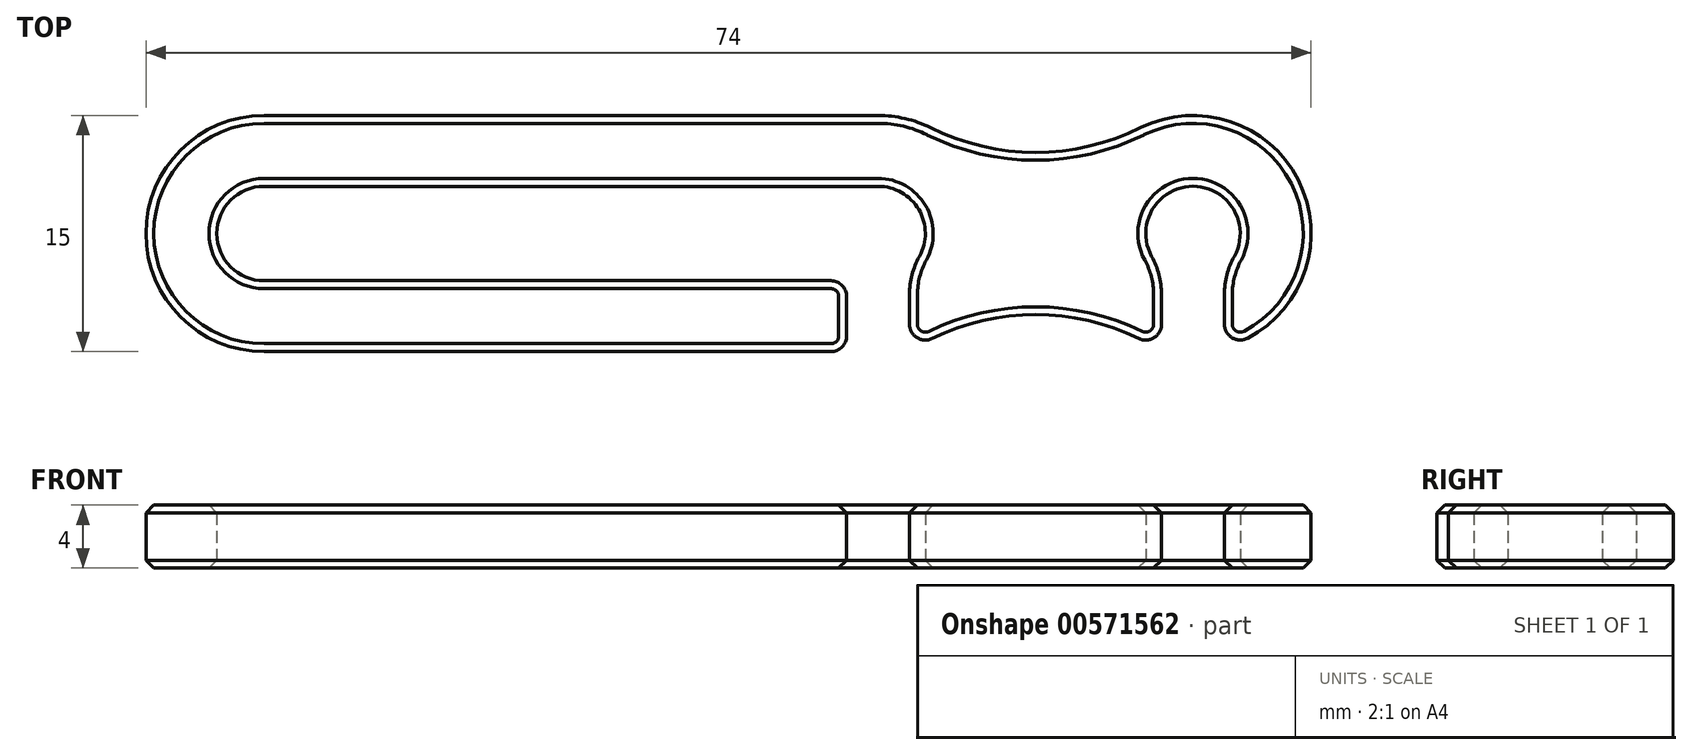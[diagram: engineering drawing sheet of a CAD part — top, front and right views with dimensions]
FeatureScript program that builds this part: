
annotation { "Feature Type Name" : "Feature", "Feature Type Description" : "" }
export const myFeature = defineFeature(function(context is Context, id is Id, definition is map)
    precondition{}
    {
        {
            var Q0;
            Q0=qCreatedBy(makeId("Top.planeOp"),FACE);
            var sketch = newSketch(context, id + "F0", { "sketchPlane" : qUnion([Q0])});
            skArc(sketch, "E0", {"start": v(2, -2.24) * mm, "mid": v(2.8, 1.07) * mm, "end": v(0, 3) * mm});
            skArc(sketch, "E1", {"start": v(-39, 3) * mm, "mid": v(-42, 0) * mm, "end": v(-39, -3) * mm});
            skArc(sketch, "E2", {"start": v(22, -2.24) * mm, "mid": v(20, 3) * mm, "end": v(18, -2.24) * mm});
            skLineSegment(sketch, "E3", {"start": v(23, 6.87) * mm, "end": v(23, -6.87) * mm, "construction": true});
            skLineSegment(sketch, "E4", {"start": v(-42, 6.87) * mm, "end": v(-42, -6.87) * mm, "construction": true});
            skLineSegment(sketch, "E5", {"start": v(-3, 7.5) * mm, "end": v(-3, -7.5) * mm, "construction": true});
            skLineSegment(sketch, "E6", {"start": v(0, 0) * mm, "end": v(-39, 0) * mm, "construction": true});
            skLineSegment(sketch, "E7", {"start": v(0, 0) * mm, "end": v(20, 0) * mm, "construction": true});
            skArc(sketch, "E8", {"start": v(3.33, 6.72) * mm, "mid": v(1.71, 7.3) * mm, "end": v(0, 7.5) * mm, "construction": true});
            skArc(sketch, "E9", {"start": v(16.67, -6.72) * mm, "mid": v(17.32, -7) * mm, "end": v(18, -7.23) * mm, "construction": true});
            skArc(sketch, "E10", {"start": v(-39, 7.5) * mm, "mid": v(-46.5, 0) * mm, "end": v(-39, -7.5) * mm, "construction": true});
            skArc(sketch, "E11", {"start": v(3.33, 6.72) * mm, "mid": v(10, 5.16) * mm, "end": v(16.67, 6.72) * mm, "construction": true});
            skArc(sketch, "E12", {"start": v(16.67, -6.72) * mm, "mid": v(10, -5.16) * mm, "end": v(3.33, -6.72) * mm, "construction": true});
            skLineSegment(sketch, "E13", {"start": v(-39, 7.5) * mm, "end": v(0, 7.5) * mm, "construction": true});
            skLineSegment(sketch, "E14", {"start": v(0, -7.5) * mm, "end": v(-39, -7.5) * mm, "construction": true});
            skArc(sketch, "E15.trimOffspring", {"start": v(0, -7.5) * mm, "mid": v(1.71, -7.3) * mm, "end": v(3.33, -6.72) * mm, "construction": true});
            skLineSegment(sketch, "E16", {"start": v(2, -2.24) * mm, "end": v(2, -7.23) * mm});
            skLineSegment(sketch, "E17", {"start": v(-2, -3) * mm, "end": v(-2, -7.5) * mm});
            skLineSegment(sketch, "E18", {"start": v(0, 0) * mm, "end": v(0, -7.5) * mm, "construction": true});
            skLineSegment(sketch, "E19", {"start": v(-2, -3) * mm, "end": v(-39, -3) * mm});
            skLineSegment(sketch, "E20", {"start": v(-39, 3) * mm, "end": v(0, 3) * mm});
            skPoint(sketch, "E21.orphan", {"position": v(0, -3) * mm});
            skPoint(sketch, "E22.orphan", {"position": v(-2, -2.24) * mm});
            skLineSegment(sketch, "E23", {"start": v(-2, -7.5) * mm, "end": v(-39, -7.5) * mm});
            skLineSegment(sketch, "E24", {"start": v(-39, 7.5) * mm, "end": v(0, 7.5) * mm});
            skArc(sketch, "E25", {"start": v(3.33, 6.72) * mm, "mid": v(1.71, 7.3) * mm, "end": v(0, 7.5) * mm});
            skArc(sketch, "E26", {"start": v(3.33, 6.72) * mm, "mid": v(10, 5.16) * mm, "end": v(16.67, 6.72) * mm});
            skArc(sketch, "E27", {"start": v(16.67, -6.72) * mm, "mid": v(17.32, -7) * mm, "end": v(18, -7.23) * mm});
            skArc(sketch, "E28", {"start": v(16.67, -6.72) * mm, "mid": v(10, -5.16) * mm, "end": v(3.33, -6.72) * mm});
            skArc(sketch, "E29", {"start": v(2, -7.23) * mm, "mid": v(2.68, -7) * mm, "end": v(3.33, -6.72) * mm});
            skArc(sketch, "E30", {"start": v(-39, 7.5) * mm, "mid": v(-46.5, 0) * mm, "end": v(-39, -7.5) * mm});
            skLineSegment(sketch, "E31", {"start": v(20, 0) * mm, "end": v(20, -7.5) * mm, "construction": true});
            skLineSegment(sketch, "E32", {"start": v(18, -2.24) * mm, "end": v(18, -7.23) * mm});
            skLineSegment(sketch, "E33", {"start": v(22, -2.24) * mm, "end": v(22, -7.23) * mm});
            skArc(sketch, "E34.trimOffspring", {"start": v(22, -7.23) * mm, "mid": v(27, 2.68) * mm, "end": v(16.67, 6.72) * mm, "construction": true});
            skArc(sketch, "E35.trimOffspring", {"start": v(22, -7.23) * mm, "mid": v(27, 2.68) * mm, "end": v(16.67, 6.72) * mm});
            skLineSegment(sketch, "E36", {"start": v(27.5, 11.34) * mm, "end": v(27.5, -10.06) * mm, "construction": true});
            skLineSegment(sketch, "E37", {"start": v(-46.5, 12.68) * mm, "end": v(-46.5, -19.11) * mm, "construction": true});
            skSolve(sketch);
        }
        {
            var Q0;
            Q0=makeQuery(id+"F0.imprint","IMPRINT",FACE,{"disambiguationData":[TD([[makeQuery(id+"F0.imprint","IMPRINT",EDGE,{"derivedFrom":sQuery(id+"F0.wireOp",EDGE,"E0")}),-1.0]])]});
            extrude(context, id + "F1", {"entities" : qUnion([Q0]), "depth" : 4 * mm, "offsetDistance" : 25 * mm});
        }
        {
            var Q0;
            Q0=makeQuery(id+"F1.opExtrude","SWEPT_EDGE",EDGE,{"disambiguationData":[OSD([sQuery(id+"F0.wireOp",EDGE,"E0"),sQuery(id+"F0.wireOp",EDGE,"E16")])]});
            var Q1;
            Q1=makeQuery(id+"F1.opExtrude","SWEPT_EDGE",EDGE,{"disambiguationData":[OSD([sQuery(id+"F0.wireOp",EDGE,"E2"),sQuery(id+"F0.wireOp",EDGE,"E32")])]});
            var Q2;
            Q2=makeQuery(id+"F1.opExtrude","SWEPT_EDGE",EDGE,{"disambiguationData":[OSD([sQuery(id+"F0.wireOp",EDGE,"E2"),sQuery(id+"F0.wireOp",EDGE,"E33")])]});
            fillet(context, id + "F2", {"entities" : qUnion([Q0, Q1, Q2]), "radius" : 5 * mm, "tangentPropagation" : true, "allowEdgeOverflow" : false});
        }
        {
            var Q0;
            Q0=makeQuery(id+"F1.opExtrude","SWEPT_EDGE",EDGE,{"disambiguationData":[OSD([sQuery(id+"F0.wireOp",EDGE,"E17"),sQuery(id+"F0.wireOp",EDGE,"E19")])]});
            var Q1;
            Q1=makeQuery(id+"F1.opExtrude","SWEPT_EDGE",EDGE,{"disambiguationData":[OSD([sQuery(id+"F0.wireOp",EDGE,"E16"),sQuery(id+"F0.wireOp",EDGE,"E29")])]});
            var Q2;
            Q2=makeQuery(id+"F1.opExtrude","SWEPT_EDGE",EDGE,{"disambiguationData":[OSD([sQuery(id+"F0.wireOp",EDGE,"E17"),sQuery(id+"F0.wireOp",EDGE,"E23")])]});
            var Q3;
            Q3=makeQuery(id+"F1.opExtrude","SWEPT_EDGE",EDGE,{"disambiguationData":[OSD([sQuery(id+"F0.wireOp",EDGE,"E27"),sQuery(id+"F0.wireOp",EDGE,"E32")])]});
            var Q4;
            Q4=makeQuery(id+"F1.opExtrude","SWEPT_EDGE",EDGE,{"disambiguationData":[OSD([sQuery(id+"F0.wireOp",EDGE,"E33"),sQuery(id+"F0.wireOp",EDGE,"E35.trimOffspring")])]});
            fillet(context, id + "F3", {"entities" : qUnion([Q0, Q1, Q2, Q3, Q4]), "radius" : 1 * mm, "tangentPropagation" : true, "allowEdgeOverflow" : false});
        }
        {
            var Q0;
            Q0=makeQuery(id+"F1.opExtrude","CAP_EDGE",EDGE,{"disambiguationData":[OSD([sQuery(id+"F0.wireOp",EDGE,"E23")])],"isStart":false});
            var Q1;
            Q1=makeQuery(id+"F1.opExtrude","CAP_EDGE",EDGE,{"disambiguationData":[OSD([sQuery(id+"F0.wireOp",EDGE,"E23")])],"isStart":true});
            chamfer(context, id + "F4", {"entities" : qUnion([Q0, Q1]), "width" : .5 * mm, "tangentPropagation" : true});
        }
    });
